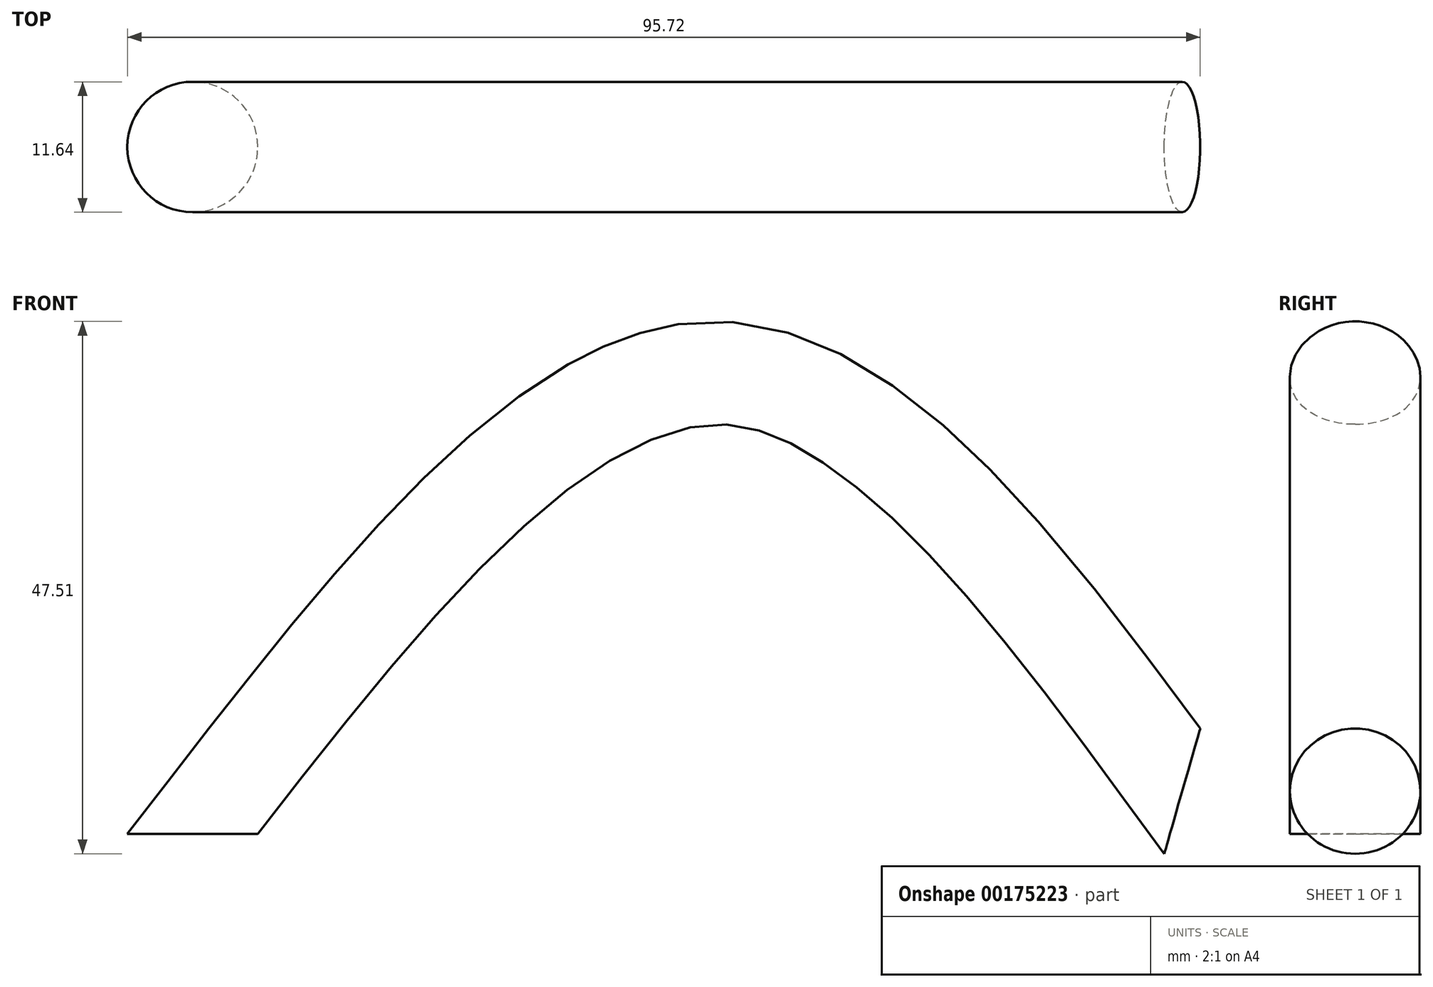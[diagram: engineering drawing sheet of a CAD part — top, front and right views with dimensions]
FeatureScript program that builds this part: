
annotation { "Feature Type Name" : "Feature", "Feature Type Description" : "" }
export const myFeature = defineFeature(function(context is Context, id is Id, definition is map)
    precondition{}
    {
        {
            var Q0;
            Q0=qCreatedBy(makeId("Front.planeOp"),FACE);
            var sketch = newSketch(context, id + "F0", { "sketchPlane" : qUnion([Q0])});
            skFitSpline(sketch, "E0", {"points": [v(-68.74, 0) * mm, v(-22.53, 40.36) * mm, v(18.83, 3.28) * mm], "startDerivative": vector(91.55, 118.43) * mm, "endDerivative": vector(83.52, -113.8) * mm});
            skSolve(sketch);
        }
        {
            var Q0;
            Q0=qCreatedBy(makeId("Top.planeOp"),FACE);
            var sketch = newSketch(context, id + "F1", { "sketchPlane" : qUnion([Q0])});
            skCircle(sketch, "E1", {"center": v(-69.31, 0) * mm, "radius": 5.82 * mm});
            skSolve(sketch);
        }
        {
            var Q0;
            Q0=makeQuery(id+"F1.imprint","IMPRINT",FACE,{"disambiguationData":[TD([[makeQuery(id+"F1.imprint","IMPRINT",EDGE,{"derivedFrom":sQuery(id+"F1.wireOp",EDGE,"E1")}),1.0]])]});
            var Q1;
            Q1=sQuery(id+"F0.wireOp",EDGE,"E0");
            sweep(context, id + "F2", {"profiles" : qUnion([Q0]), "path" : qUnion([Q1])});
        }
    });
